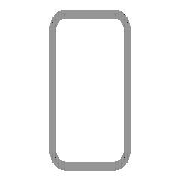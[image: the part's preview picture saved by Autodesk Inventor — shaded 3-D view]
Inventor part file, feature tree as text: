
AUTODESK INVENTOR PART (.ipt)
format: ipt  version: 2025 (Build 290162010, 162A)  size: 133,120 bytes
history: native  units: mm (DEFAULTED — no unit token found)
features: other x4, sketch x1, plane x1
ambient origin geometry x8: Origin, YZ Plane, XZ Plane, XY Plane, X Axis, Y Axis, Z Axis, Center Point
bodies: Solid1 (feature_tree), Body (feature_tree)
feature tree (6):
  parser-record x1  (decoder bookkeeping rows leaked as tree rows — omitted from the tree; the rows remain in map.json)
  other  "Driven Length"
  other  "Start Plane"
  other  "End Plane"
  sketch  "Sketch3"  dims[d3=1000.0mm d4=0.0mm d7=6.0mm d9=40.0mm d11=60.0mm d12=3.0mm d13=-0.0mm d14=1000.0mm d15=20.0mm d16=30.0mm d17=90.0deg d18=1000.0mm]
  plane  "Work Plane3"
